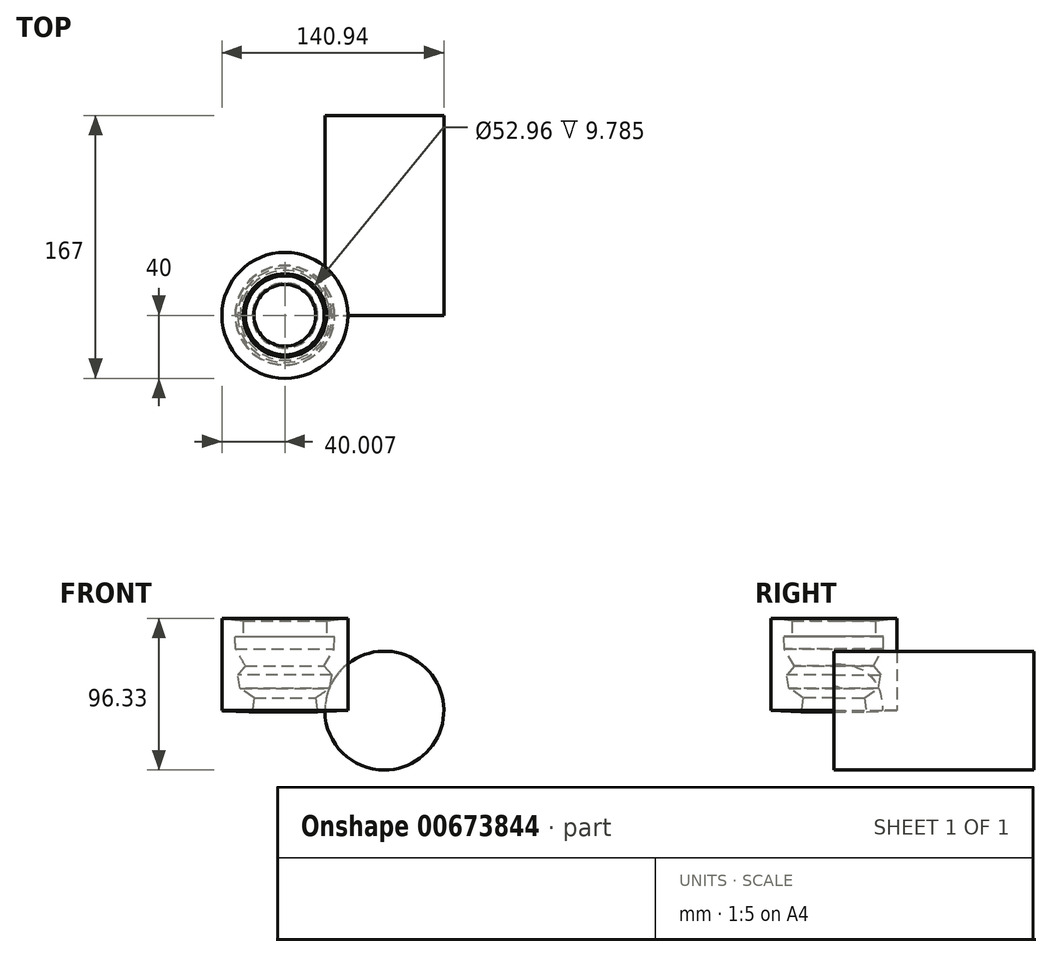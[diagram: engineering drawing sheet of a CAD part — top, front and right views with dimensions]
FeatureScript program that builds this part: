
annotation { "Feature Type Name" : "Feature", "Feature Type Description" : "" }
export const myFeature = defineFeature(function(context is Context, id is Id, definition is map)
    precondition{}
    {
        {
            var Q0;
            Q0=qCreatedBy(makeId("Front.planeOp"),FACE);
            var sketch = newSketch(context, id + "F0", { "sketchPlane" : qUnion([Q0])});
            skCircle(sketch, "E0", {"center": v(0, 0) * mm, "radius": 37.76 * mm});
            skSolve(sketch);
        }
        {
            var Q0;
            Q0=makeQuery(id+"F0.imprint","IMPRINT",FACE,{"disambiguationData":[TD([[makeQuery(id+"F0.imprint","IMPRINT",EDGE,{"derivedFrom":sQuery(id+"F0.wireOp",EDGE,"E0")}),1.0]])]});
            extrude(context, id + "F1", {"entities" : qUnion([Q0]), "oppositeDirection" : true, "depth" : 127 * mm, "offsetDistance" : 25.4 * mm});
        }
        {
            var Q0;
            Q0=qCreatedBy(makeId("Front.planeOp"),FACE);
            var sketch = newSketch(context, id + "F2", { "sketchPlane" : qUnion([Q0])});
            skLineSegment(sketch, "E1", {"start": v(-63.17, 0) * mm, "end": v(-63.17, 56.84) * mm});
            skLineSegment(sketch, "E2", {"start": v(-103.18, 0) * mm, "end": v(-103.18, 58.57) * mm});
            skLineSegment(sketch, "E3", {"start": v(-103.18, 58.57) * mm, "end": v(-89.65, 56.84) * mm});
            skLineSegment(sketch, "E4", {"start": v(-89.65, 56.84) * mm, "end": v(-89.65, 47.06) * mm});
            skLineSegment(sketch, "E5", {"start": v(-89.65, 47.06) * mm, "end": v(-94.83, 47.06) * mm});
            skLineSegment(sketch, "E6", {"start": v(-94.83, 47.06) * mm, "end": v(-94.54, 39.29) * mm});
            skLineSegment(sketch, "E7", {"start": v(-94.54, 39.29) * mm, "end": v(-88.21, 28.35) * mm});
            skLineSegment(sketch, "E8", {"start": v(-88.21, 28.35) * mm, "end": v(-93.1, 22.6) * mm});
            skLineSegment(sketch, "E9", {"start": v(-93.1, 22.6) * mm, "end": v(-91.67, 14.25) * mm});
            skLineSegment(sketch, "E10", {"start": v(-91.67, 14.25) * mm, "end": v(-82.74, 8.2) * mm});
            skLineSegment(sketch, "E11", {"start": v(-82.74, 8.2) * mm, "end": v(-83.9, -0.72) * mm});
            skLineSegment(sketch, "E12", {"start": v(-83.9, -0.72) * mm, "end": v(-103.18, 0) * mm});
            skSolve(sketch);
        }
        {
            var Q0;
            Q0=makeQuery(id+"F2.imprint","IMPRINT",FACE,{"disambiguationData":[TD([[makeQuery(id+"F2.imprint","IMPRINT",EDGE,{"derivedFrom":sQuery(id+"F2.wireOp",EDGE,"E2")}),-1.0]])]});
            var Q1;
            Q1=sQuery(id+"F2.wireOp",EDGE,"E1");
            revolve(context, id + "F3", {"operationType" : NewBodyOperationType.ADD, "entities" : qUnion([Q0]), "axis" : qUnion([Q1]), "revolveType" : RevolveType.FULL});
        }
    });
